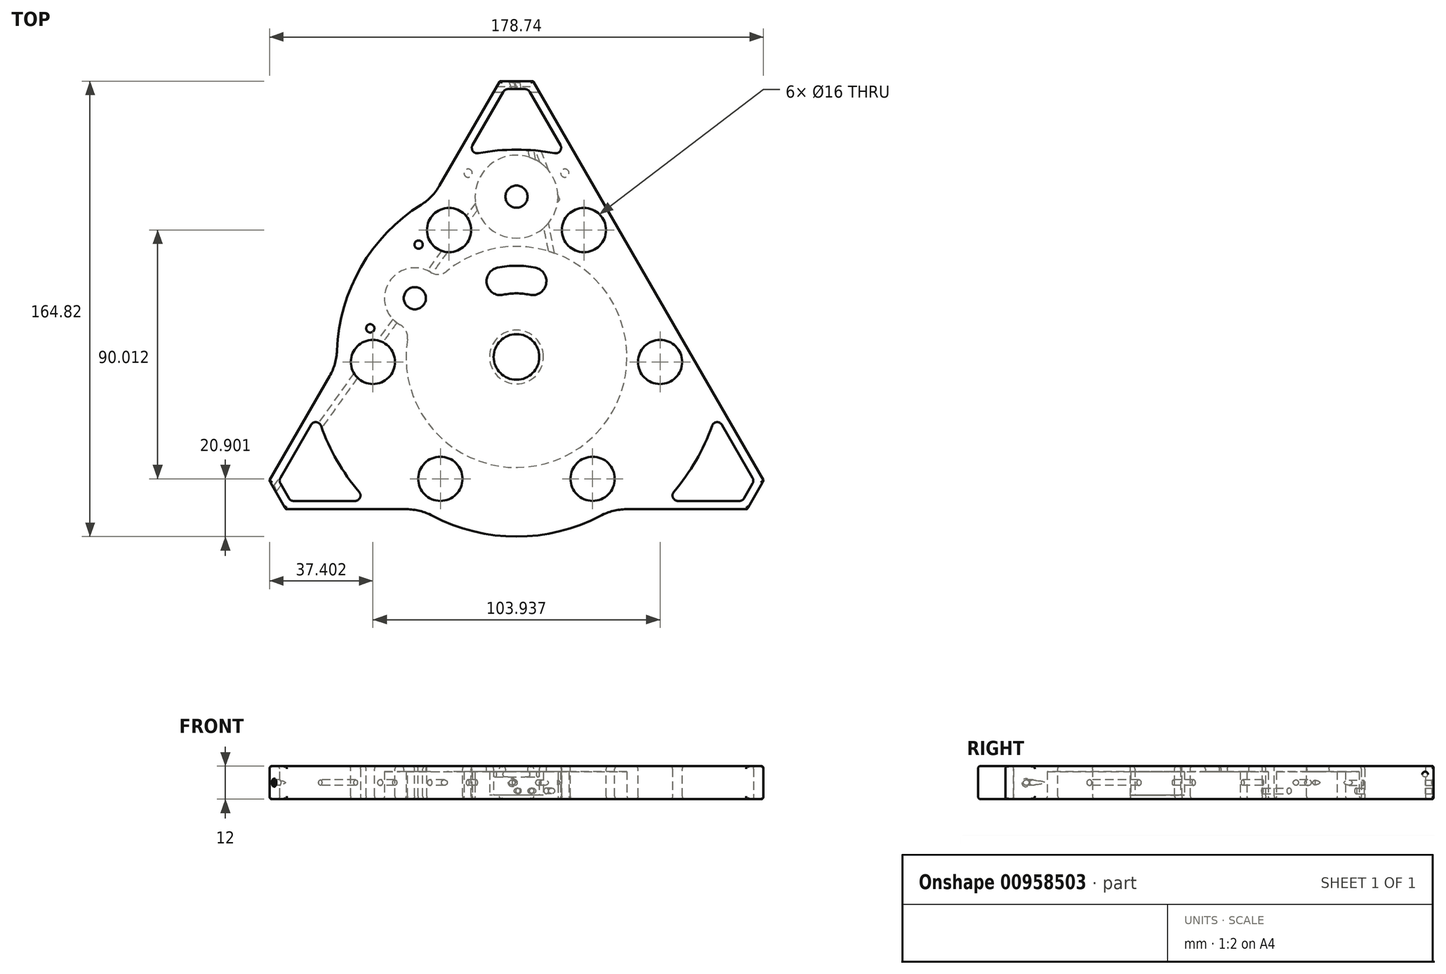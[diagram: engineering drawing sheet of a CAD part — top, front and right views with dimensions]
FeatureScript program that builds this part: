
annotation { "Feature Type Name" : "Feature", "Feature Type Description" : "" }
export const myFeature = defineFeature(function(context is Context, id is Id, definition is map)
    precondition{}
    {
        {
            var Q0;
            Q0=qCreatedBy(makeId("Top.planeOp"),FACE);
            var sketch = newSketch(context, id + "F0", { "sketchPlane" : qUnion([Q0])});
            skCircle(sketch, "E0", {"center": v(0, 0) * mm, "radius": 100 * mm, "construction": true});
            skCircle(sketch, "E1", {"center": v(0, 0) * mm, "radius": 65 * mm});
            skLineSegment(sketch, "E2", {"start": v(-6, 99.82) * mm, "end": v(-89.45, -44.71) * mm});
            skLineSegment(sketch, "E3", {"start": v(-89.45, -44.71) * mm, "end": v(-83.45, -55.1) * mm});
            skLineSegment(sketch, "E4", {"start": v(-83.45, -55.1) * mm, "end": v(83.45, -55.1) * mm});
            skLineSegment(sketch, "E5", {"start": v(83.45, -55.1) * mm, "end": v(89.45, -44.71) * mm});
            skLineSegment(sketch, "E6", {"start": v(89.45, -44.71) * mm, "end": v(6, 99.82) * mm});
            skLineSegment(sketch, "E7", {"start": v(6, 99.82) * mm, "end": v(-6, 99.82) * mm});
            skLineSegment(sketch, "E8", {"start": v(-86.6, -50) * mm, "end": v(0, 0) * mm, "construction": true});
            skLineSegment(sketch, "E9", {"start": v(0, 0) * mm, "end": v(86.45, -49.9) * mm, "construction": true});
            skCircle(sketch, "E10", {"center": v(0, 0) * mm, "radius": 75 * mm});
            skCircle(sketch, "E11", {"center": v(0, 0) * mm, "radius": 97 * mm, "construction": true});
            skLineSegment(sketch, "E12", {"start": v(-81.82, -52.1) * mm, "end": v(-53.94, -52.1) * mm});
            skLineSegment(sketch, "E13", {"start": v(-86.03, -44.8) * mm, "end": v(-72.1, -20.66) * mm});
            skLineSegment(sketch, "E14", {"start": v(-81.82, -52.1) * mm, "end": v(-86.03, -44.8) * mm});
            skLineSegment(sketch, "E15", {"start": v(81.82, -52.1) * mm, "end": v(53.94, -52.1) * mm});
            skLineSegment(sketch, "E16", {"start": v(86.03, -44.8) * mm, "end": v(72.1, -20.66) * mm});
            skLineSegment(sketch, "E17", {"start": v(86.03, -44.8) * mm, "end": v(81.82, -52.1) * mm});
            skLineSegment(sketch, "E18", {"start": v(-18.15, 72.77) * mm, "end": v(-4.22, 96.9) * mm});
            skLineSegment(sketch, "E19", {"start": v(18.15, 72.77) * mm, "end": v(4.22, 96.9) * mm});
            skLineSegment(sketch, "E20", {"start": v(4.22, 96.9) * mm, "end": v(-4.22, 96.9) * mm});
            skSolve(sketch);
        }
        {
            var Q0;
            {var subQ0=sQuery(id+"F0.wireOp",EDGE,"E2");var subQ1=sQuery(id+"F0.wireOp",EDGE,"E1");var subQ2=makeQuery(id+"F0.imprint","INTERSECT",VERTEX,{"disambiguationData":[OD(0.0)],"derivedFrom":[subQ1,subQ0]});Q0=makeQuery(id+"F0.imprint","IMPRINT",FACE,{"disambiguationData":[TD([[makeQuery(id+"F0.imprint","IMPRINT",EDGE,{"disambiguationData":[TD([[subQ2,1.0]])],"derivedFrom":subQ1}),1.0]])]});}
            var Q1;
            {var subQ2=sQuery(id+"F0.wireOp",EDGE,"E2");var subQ6=sQuery(id+"F0.wireOp",EDGE,"E1");var subQ8=makeQuery(id+"F0.imprint","INTERSECT",VERTEX,{"disambiguationData":[OD(1.0)],"derivedFrom":[subQ6,subQ2]});Q1=makeQuery(id+"F0.imprint","IMPRINT",FACE,{"disambiguationData":[TD([[makeQuery(id+"F0.imprint","IMPRINT",EDGE,{"disambiguationData":[TD([[subQ8,-1.0]])],"derivedFrom":subQ6}),-1.0]])]});}
            var Q2;
            {var subQ0=sQuery(id+"F0.wireOp",EDGE,"E4");var subQ1=sQuery(id+"F0.wireOp",EDGE,"E1");var subQ2=makeQuery(id+"F0.imprint","INTERSECT",VERTEX,{"disambiguationData":[OD(0.0)],"derivedFrom":[subQ1,subQ0]});Q2=makeQuery(id+"F0.imprint","IMPRINT",FACE,{"disambiguationData":[TD([[makeQuery(id+"F0.imprint","IMPRINT",EDGE,{"disambiguationData":[TD([[subQ2,-1.0]])],"derivedFrom":subQ1}),1.0]])]});}
            var Q3;
            {var subQ5=sQuery(id+"F0.wireOp",EDGE,"E3");Q3=makeQuery(id+"F0.imprint","IMPRINT",FACE,{"disambiguationData":[TD([[makeQuery(id+"F0.imprint","IMPRINT",EDGE,{"derivedFrom":subQ5}),1.0]])]});}
            var Q4;
            {var subQ0=sQuery(id+"F0.wireOp",EDGE,"E2");var subQ1=sQuery(id+"F0.wireOp",EDGE,"E1");var subQ2=makeQuery(id+"F0.imprint","INTERSECT",VERTEX,{"disambiguationData":[OD(0.0)],"derivedFrom":[subQ1,subQ0]});Q4=makeQuery(id+"F0.imprint","IMPRINT",FACE,{"disambiguationData":[TD([[makeQuery(id+"F0.imprint","IMPRINT",EDGE,{"disambiguationData":[TD([[subQ2,-1.0]])],"derivedFrom":subQ1}),1.0]])]});}
            var Q5;
            {var subQ4=sQuery(id+"F0.wireOp",EDGE,"E7");Q5=makeQuery(id+"F0.imprint","IMPRINT",FACE,{"disambiguationData":[TD([[makeQuery(id+"F0.imprint","IMPRINT",EDGE,{"derivedFrom":subQ4}),1.0]])]});}
            var Q6;
            {var subQ4=sQuery(id+"F0.wireOp",EDGE,"E1");var subQ6=sQuery(id+"F0.wireOp",EDGE,"E2");var subQ8=makeQuery(id+"F0.imprint","INTERSECT",VERTEX,{"disambiguationData":[OD(0.0)],"derivedFrom":[subQ4,subQ6]});Q6=makeQuery(id+"F0.imprint","IMPRINT",FACE,{"disambiguationData":[TD([[makeQuery(id+"F0.imprint","IMPRINT",EDGE,{"disambiguationData":[TD([[subQ8,1.0]])],"derivedFrom":subQ4}),-1.0]])]});}
            var Q7;
            {var subQ1=sQuery(id+"F0.wireOp",EDGE,"E5");Q7=makeQuery(id+"F0.imprint","IMPRINT",FACE,{"disambiguationData":[TD([[makeQuery(id+"F0.imprint","IMPRINT",EDGE,{"derivedFrom":subQ1}),1.0]])]});}
            var Q8;
            {var subQ2=sQuery(id+"F0.wireOp",EDGE,"E4");var subQ4=sQuery(id+"F0.wireOp",EDGE,"E1");var subQ5=makeQuery(id+"F0.imprint","INTERSECT",VERTEX,{"disambiguationData":[OD(1.0)],"derivedFrom":[subQ4,subQ2]});Q8=makeQuery(id+"F0.imprint","IMPRINT",FACE,{"disambiguationData":[TD([[makeQuery(id+"F0.imprint","IMPRINT",EDGE,{"disambiguationData":[TD([[subQ5,-1.0]])],"derivedFrom":subQ4}),-1.0]])]});}
            var Q9;
            {var subQ0=sQuery(id+"F0.wireOp",EDGE,"E6");var subQ1=sQuery(id+"F0.wireOp",EDGE,"E1");var subQ2=makeQuery(id+"F0.imprint","INTERSECT",VERTEX,{"disambiguationData":[OD(0.0)],"derivedFrom":[subQ1,subQ0]});Q9=makeQuery(id+"F0.imprint","IMPRINT",FACE,{"disambiguationData":[TD([[makeQuery(id+"F0.imprint","IMPRINT",EDGE,{"disambiguationData":[TD([[subQ2,1.0]])],"derivedFrom":subQ1}),1.0]])]});}
            extrude(context, id + "F1", {"entities" : qUnion([Q0, Q1, Q2, Q3, Q4, Q5, Q6, Q7, Q8, Q9]), "depth" : 12 * mm, "offsetDistance" : 25 * mm});
        }
        {
            var Q0;
            Q0=makeQuery(id+"F1.opExtrude","SWEPT_EDGE",EDGE,{"disambiguationData":[OSD([sQuery(id+"F0.wireOp",EDGE,"E10"),sQuery(id+"F0.wireOp",EDGE,"E13")])]});
            var Q1;
            Q1=makeQuery(id+"F1.opExtrude","SWEPT_EDGE",EDGE,{"disambiguationData":[OSD([sQuery(id+"F0.wireOp",EDGE,"E10"),sQuery(id+"F0.wireOp",EDGE,"E12")])]});
            var Q2;
            Q2=makeQuery(id+"F1.opExtrude","SWEPT_EDGE",EDGE,{"disambiguationData":[OSD([sQuery(id+"F0.wireOp",EDGE,"E13"),sQuery(id+"F0.wireOp",EDGE,"E14")])]});
            var Q3;
            Q3=makeQuery(id+"F1.opExtrude","SWEPT_EDGE",EDGE,{"disambiguationData":[OSD([sQuery(id+"F0.wireOp",EDGE,"E12"),sQuery(id+"F0.wireOp",EDGE,"E14")])]});
            var Q4;
            Q4=makeQuery(id+"F1.opExtrude","SWEPT_EDGE",EDGE,{"disambiguationData":[OSD([sQuery(id+"F0.wireOp",EDGE,"E10"),sQuery(id+"F0.wireOp",EDGE,"E18")])]});
            var Q5;
            Q5=makeQuery(id+"F1.opExtrude","SWEPT_EDGE",EDGE,{"disambiguationData":[OSD([sQuery(id+"F0.wireOp",EDGE,"E10"),sQuery(id+"F0.wireOp",EDGE,"E19")])]});
            var Q6;
            Q6=makeQuery(id+"F1.opExtrude","SWEPT_EDGE",EDGE,{"disambiguationData":[OSD([sQuery(id+"F0.wireOp",EDGE,"E19"),sQuery(id+"F0.wireOp",EDGE,"E20")])]});
            var Q7;
            Q7=makeQuery(id+"F1.opExtrude","SWEPT_EDGE",EDGE,{"disambiguationData":[OSD([sQuery(id+"F0.wireOp",EDGE,"E18"),sQuery(id+"F0.wireOp",EDGE,"E20")])]});
            var Q8;
            Q8=makeQuery(id+"F1.opExtrude","SWEPT_EDGE",EDGE,{"disambiguationData":[OSD([sQuery(id+"F0.wireOp",EDGE,"E10"),sQuery(id+"F0.wireOp",EDGE,"E16")])]});
            var Q9;
            Q9=makeQuery(id+"F1.opExtrude","SWEPT_EDGE",EDGE,{"disambiguationData":[OSD([sQuery(id+"F0.wireOp",EDGE,"E10"),sQuery(id+"F0.wireOp",EDGE,"E15")])]});
            var Q10;
            Q10=makeQuery(id+"F1.opExtrude","SWEPT_EDGE",EDGE,{"disambiguationData":[OSD([sQuery(id+"F0.wireOp",EDGE,"E15"),sQuery(id+"F0.wireOp",EDGE,"E17")])]});
            var Q11;
            Q11=makeQuery(id+"F1.opExtrude","SWEPT_EDGE",EDGE,{"disambiguationData":[OSD([sQuery(id+"F0.wireOp",EDGE,"E16"),sQuery(id+"F0.wireOp",EDGE,"E17")])]});
            fillet(context, id + "F2", {"entities" : qUnion([Q0, Q1, Q2, Q3, Q4, Q5, Q6, Q7, Q8, Q9, Q10, Q11]), "radius" : 2 * mm, "tangentPropagation" : true, "allowEdgeOverflow" : false});
        }
        {
            var Q0;
            Q0=qCreatedBy(makeId("Top.planeOp"),FACE);
            var sketch = newSketch(context, id + "F3", { "sketchPlane" : qUnion([Q0])});
            skCircle(sketch, "E21", {"center": v(0, 0) * mm, "radius": 8.25 * mm});
            skSolve(sketch);
        }
        {
            var Q0;
            Q0=qSketchRegion(id+"F3",true);
            extrude(context, id + "F4", {"entities" : qUnion([Q0]), "operationType" : NewBodyOperationType.REMOVE, "depth" : 100 * mm, "offsetDistance" : 25 * mm});
        }
        {
            var Q0;
            Q0=qCreatedBy(makeId("Top.planeOp"),FACE);
            var sketch = newSketch(context, id + "F5", { "sketchPlane" : qUnion([Q0])});
            skCircle(sketch, "E22", {"center": v(0, 58) * mm, "radius": 15 * mm});
            skCircle(sketch, "E23", {"center": v(-17.5, 66.5) * mm, "radius": 1.5 * mm});
            skCircle(sketch, "E24", {"center": v(17.5, 66.5) * mm, "radius": 1.5 * mm});
            skCircle(sketch, "E25", {"center": v(0, 58) * mm, "radius": 4 * mm});
            skSolve(sketch);
        }
        {
            var Q0;
            Q0=makeQuery(id+"F5.imprint","IMPRINT",FACE,{"disambiguationData":[TD([[makeQuery(id+"F5.imprint","IMPRINT",EDGE,{"derivedFrom":sQuery(id+"F5.wireOp",EDGE,"E25")}),1.0]])]});
            var Q1;
            Q1=makeQuery(id+"F5.imprint","IMPRINT",FACE,{"disambiguationData":[TD([[makeQuery(id+"F5.imprint","IMPRINT",EDGE,{"derivedFrom":sQuery(id+"F5.wireOp",EDGE,"E22")}),1.0]])]});
            var Q2;
            Q2=makeQuery(id+"F5.imprint","IMPRINT",FACE,{"disambiguationData":[TD([[makeQuery(id+"F5.imprint","IMPRINT",EDGE,{"derivedFrom":sQuery(id+"F5.wireOp",EDGE,"E24")}),1.0]])]});
            var Q3;
            Q3=makeQuery(id+"F5.imprint","IMPRINT",FACE,{"disambiguationData":[TD([[makeQuery(id+"F5.imprint","IMPRINT",EDGE,{"derivedFrom":sQuery(id+"F5.wireOp",EDGE,"E23")}),1.0]])]});
            extrude(context, id + "F6", {"entities" : qUnion([Q0, Q1, Q2, Q3]), "operationType" : NewBodyOperationType.REMOVE, "depth" : 10 * mm, "offsetDistance" : 25 * mm});
        }
        {
            var Q0;
            Q0=makeQuery(id+"F5.imprint","IMPRINT",FACE,{"disambiguationData":[TD([[makeQuery(id+"F5.imprint","IMPRINT",EDGE,{"derivedFrom":sQuery(id+"F5.wireOp",EDGE,"E25")}),1.0]])]});
            extrude(context, id + "F7", {"entities" : qUnion([Q0]), "operationType" : NewBodyOperationType.REMOVE, "depth" : 25 * mm, "offsetDistance" : 25 * mm});
        }
        {
            var Q0;
            Q0=qCreatedBy(makeId("Top.planeOp"),FACE);
            var sketch = newSketch(context, id + "F8", { "sketchPlane" : qUnion([Q0])});
            skCircle(sketch, "E26", {"center": v(0, 0) * mm, "radius": 40 * mm});
            skCircle(sketch, "E27", {"center": v(0, 0) * mm, "radius": 9.75 * mm});
            skSolve(sketch);
        }
        {
            var Q0;
            Q0=qSketchRegion(id+"F8",true);
            extrude(context, id + "F9", {"entities" : qUnion([Q0]), "operationType" : NewBodyOperationType.REMOVE, "depth" : 10 * mm, "offsetDistance" : 25 * mm});
        }
        {
            var Q0;
            Q0=qCreatedBy(makeId("Top.planeOp"),FACE);
            var sketch = newSketch(context, id + "F10", { "sketchPlane" : qUnion([Q0])});
            skCircle(sketch, "E28", {"center": v(-36.8, 21.25) * mm, "radius": 11 * mm});
            skLineSegment(sketch, "E29", {"start": v(-36.8, 21.25) * mm, "end": v(0, 0) * mm, "construction": true});
            skCircle(sketch, "E30", {"center": v(-36.8, 21.25) * mm, "radius": 4 * mm});
            skSolve(sketch);
        }
        {
            var Q0;
            Q0=makeQuery(id+"F10.imprint","IMPRINT",FACE,{"disambiguationData":[TD([[makeQuery(id+"F10.imprint","IMPRINT",EDGE,{"derivedFrom":sQuery(id+"F10.wireOp",EDGE,"E28")}),1.0]])]});
            var Q1;
            Q1=makeQuery(id+"F10.imprint","IMPRINT",FACE,{"disambiguationData":[TD([[makeQuery(id+"F10.imprint","IMPRINT",EDGE,{"derivedFrom":sQuery(id+"F10.wireOp",EDGE,"E30")}),1.0]])]});
            extrude(context, id + "F11", {"entities" : qUnion([Q0, Q1]), "operationType" : NewBodyOperationType.REMOVE, "depth" : 10 * mm, "offsetDistance" : 25 * mm});
        }
        {
            var Q0;
            Q0=makeQuery(id+"F10.imprint","IMPRINT",FACE,{"disambiguationData":[TD([[makeQuery(id+"F10.imprint","IMPRINT",EDGE,{"derivedFrom":sQuery(id+"F10.wireOp",EDGE,"E30")}),1.0]])]});
            extrude(context, id + "F12", {"entities" : qUnion([Q0]), "operationType" : NewBodyOperationType.REMOVE, "depth" : 25 * mm, "offsetDistance" : 25 * mm});
        }
        {
            var Q0;
            Q0=qCreatedBy(makeId("Top.planeOp"),FACE);
            var sketch = newSketch(context, id + "F13", { "sketchPlane" : qUnion([Q0])});
            skLineSegment(sketch, "E31", {"start": v(0, 0) * mm, "end": v(-36.8, 21.25) * mm, "construction": true});
            skLineSegment(sketch, "E32", {"start": v(-35.42, 40.66) * mm, "end": v(-52.92, 10.34) * mm, "construction": true});
            skCircle(sketch, "E33", {"center": v(-35.42, 40.66) * mm, "radius": 1.5 * mm});
            skCircle(sketch, "E34", {"center": v(-52.92, 10.34) * mm, "radius": 1.5 * mm});
            skCircle(sketch, "E35", {"center": v(-35.42, 40.66) * mm, "radius": 4 * mm});
            skCircle(sketch, "E36", {"center": v(-52.92, 10.34) * mm, "radius": 4 * mm});
            skSolve(sketch);
        }
        {
            var Q0;
            Q0=makeQuery(id+"F13.imprint","IMPRINT",FACE,{"disambiguationData":[TD([[makeQuery(id+"F13.imprint","IMPRINT",EDGE,{"derivedFrom":sQuery(id+"F13.wireOp",EDGE,"E33")}),1.0]])]});
            var Q1;
            Q1=makeQuery(id+"F13.imprint","IMPRINT",FACE,{"disambiguationData":[TD([[makeQuery(id+"F13.imprint","IMPRINT",EDGE,{"derivedFrom":sQuery(id+"F13.wireOp",EDGE,"E34")}),1.0]])]});
            extrude(context, id + "F14", {"entities" : qUnion([Q0, Q1]), "operationType" : NewBodyOperationType.REMOVE, "endBound" : BoundingType.SYMMETRIC, "oppositeDirection" : true, "depth" : 100 * mm, "offsetDistance" : 25 * mm});
        }
        {
            var Q0;
            Q0=qCreatedBy(makeId("Top.planeOp"),FACE);
            cPlane(context, id + "F15", {"entities" : qUnion([Q0]), "cplaneType" : CPlaneType.OFFSET, "offset" : 3 * mm, "width" : 150 * mm, "height" : 150 * mm});
        }
        {
            var Q0;
            Q0=makeQuery(id+"F11.boolean.opBoolean","INTERSECT",EDGE,{"disambiguationData":[OD(1.0)],"derivedFrom":[makeQuery(id+"F9.boolean.opBoolean","COPY",FACE,{"derivedFrom":makeQuery(id+"F9.opExtrude","SWEPT_FACE",FACE,{"disambiguationData":[OSD([sQuery(id+"F8.wireOp",EDGE,"E26")])]})}),makeQuery(id+"F11.opExtrude","SWEPT_FACE",FACE,{"disambiguationData":[OSD([sQuery(id+"F10.wireOp",EDGE,"E28")])]})]});
            var Q1;
            Q1=makeQuery(id+"F11.boolean.opBoolean","INTERSECT",EDGE,{"disambiguationData":[OD(0.0)],"derivedFrom":[makeQuery(id+"F9.boolean.opBoolean","COPY",FACE,{"derivedFrom":makeQuery(id+"F9.opExtrude","SWEPT_FACE",FACE,{"disambiguationData":[OSD([sQuery(id+"F8.wireOp",EDGE,"E26")])]})}),makeQuery(id+"F11.opExtrude","SWEPT_FACE",FACE,{"disambiguationData":[OSD([sQuery(id+"F10.wireOp",EDGE,"E28")])]})]});
            var Q2;
            Q2=makeQuery(id+"FJ90VYnbGjNsUTn_1.2.F11.boolean.opBoolean","INTERSECT",EDGE,{"disambiguationData":[OD(0.0)],"derivedFrom":[makeQuery(id+"FJ90VYnbGjNsUTn_1.1.F11.boolean.opBoolean","SPLIT",FACE,{"disambiguationData":[OD(1.0)],"derivedFrom":makeQuery(id+"F9.boolean.opBoolean","COPY",FACE,{"derivedFrom":makeQuery(id+"F9.opExtrude","SWEPT_FACE",FACE,{"disambiguationData":[OSD([sQuery(id+"F8.wireOp",EDGE,"E26")])]})})}),makeQuery(id+"FJ90VYnbGjNsUTn_1.2.F11.opExtrude","SWEPT_FACE",FACE,{"disambiguationData":[OSD([sQuery(id+"F10.wireOp",EDGE,"E28")])]})]});
            var Q3;
            Q3=makeQuery(id+"FJ90VYnbGjNsUTn_1.2.F11.boolean.opBoolean","INTERSECT",EDGE,{"disambiguationData":[OD(1.0)],"derivedFrom":[makeQuery(id+"FJ90VYnbGjNsUTn_1.1.F11.boolean.opBoolean","SPLIT",FACE,{"disambiguationData":[OD(1.0)],"derivedFrom":makeQuery(id+"F9.boolean.opBoolean","COPY",FACE,{"derivedFrom":makeQuery(id+"F9.opExtrude","SWEPT_FACE",FACE,{"disambiguationData":[OSD([sQuery(id+"F8.wireOp",EDGE,"E26")])]})})}),makeQuery(id+"FJ90VYnbGjNsUTn_1.2.F11.opExtrude","SWEPT_FACE",FACE,{"disambiguationData":[OSD([sQuery(id+"F10.wireOp",EDGE,"E28")])]})]});
            var Q4;
            Q4=makeQuery(id+"FJ90VYnbGjNsUTn_1.1.F11.boolean.opBoolean","INTERSECT",EDGE,{"disambiguationData":[OD(1.0)],"derivedFrom":[makeQuery(id+"F9.boolean.opBoolean","COPY",FACE,{"derivedFrom":makeQuery(id+"F9.opExtrude","SWEPT_FACE",FACE,{"disambiguationData":[OSD([sQuery(id+"F8.wireOp",EDGE,"E26")])]})}),makeQuery(id+"FJ90VYnbGjNsUTn_1.1.F11.opExtrude","SWEPT_FACE",FACE,{"disambiguationData":[OSD([sQuery(id+"F10.wireOp",EDGE,"E28")])]})]});
            var Q5;
            Q5=makeQuery(id+"FJ90VYnbGjNsUTn_1.1.F11.boolean.opBoolean","INTERSECT",EDGE,{"disambiguationData":[OD(0.0)],"derivedFrom":[makeQuery(id+"F9.boolean.opBoolean","COPY",FACE,{"derivedFrom":makeQuery(id+"F9.opExtrude","SWEPT_FACE",FACE,{"disambiguationData":[OSD([sQuery(id+"F8.wireOp",EDGE,"E26")])]})}),makeQuery(id+"FJ90VYnbGjNsUTn_1.1.F11.opExtrude","SWEPT_FACE",FACE,{"disambiguationData":[OSD([sQuery(id+"F10.wireOp",EDGE,"E28")])]})]});
            fillet(context, id + "F16", {"entities" : qUnion([Q0, Q1, Q2, Q3, Q4, Q5]), "radius" : 5 * mm, "tangentPropagation" : true, "allowEdgeOverflow" : false});
        }
        {
            var Q0;
            Q0=qCreatedBy(id+"F15.planeOp",FACE);
            var sketch = newSketch(context, id + "F17", { "sketchPlane" : qUnion([Q0])});
            skCircle(sketch, "E37", {"center": v(0, 0) * mm, "radius": 20 * mm, "construction": true});
            skLineSegment(sketch, "E38", {"start": v(19.6, 3.98) * mm, "end": v(0, 100.5) * mm});
            skCircle(sketch, "E39", {"center": v(0, 0) * mm, "radius": 100.5 * mm, "construction": true});
            skLineSegment(sketch, "E40", {"start": v(19.6, 3.98) * mm, "end": v(20.58, 4.18) * mm});
            skLineSegment(sketch, "E41", {"start": v(20.58, 4.18) * mm, "end": v(0.98, 100.7) * mm});
            skLineSegment(sketch, "E42", {"start": v(0.98, 100.7) * mm, "end": v(0, 100.5) * mm});
            skSolve(sketch);
        }
        {
            var Q0;
            Q0=makeQuery(id+"F17.imprint","IMPRINT",FACE,{"disambiguationData":[TD([[makeQuery(id+"F17.imprint","IMPRINT",EDGE,{"derivedFrom":sQuery(id+"F17.wireOp",EDGE,"E38")}),-1.0]])]});
            var Q1;
            Q1=sQuery(id+"F17.wireOp",EDGE,"E38");
            revolve(context, id + "F18", {"operationType" : NewBodyOperationType.REMOVE, "surfaceOperationType" : NewSurfaceOperationType.NEW, "entities" : qUnion([Q0]), "axis" : qUnion([Q1]), "revolveType" : RevolveType.FULL, "oppositeDirection" : true});
        }
        {
            var Q0;
            Q0=qCreatedBy(makeId("Top.planeOp"),FACE);
            cPlane(context, id + "F19", {"entities" : qUnion([Q0]), "cplaneType" : CPlaneType.OFFSET, "offset" : 6 * mm, "width" : 150 * mm, "height" : 150 * mm});
        }
        {
            var Q0;
            Q0=qCreatedBy(id+"F19.planeOp",FACE);
            var sketch = newSketch(context, id + "F20", { "sketchPlane" : qUnion([Q0])});
            skCircle(sketch, "E43", {"center": v(0, 0) * mm, "radius": 58 * mm, "construction": true});
            skCircle(sketch, "E44", {"center": v(0, 0) * mm, "radius": 100.5 * mm, "construction": true});
            skLineSegment(sketch, "E45", {"start": v(15, 56.03) * mm, "end": v(-2, 100.48) * mm});
            skLineSegment(sketch, "E46", {"start": v(-2, 100.48) * mm, "end": v(-3, 100.46) * mm});
            skLineSegment(sketch, "E47", {"start": v(-3, 100.46) * mm, "end": v(13.88, 56.31) * mm});
            skLineSegment(sketch, "E48", {"start": v(13.88, 56.31) * mm, "end": v(15, 56.03) * mm});
            skLineSegment(sketch, "E49", {"start": v(-13, 56.52) * mm, "end": v(-88.02, -48.5) * mm});
            skLineSegment(sketch, "E50", {"start": v(-88.02, -48.5) * mm, "end": v(-88.55, -47.53) * mm});
            skLineSegment(sketch, "E51", {"start": v(-88.55, -47.53) * mm, "end": v(-14.49, 56.16) * mm});
            skLineSegment(sketch, "E52", {"start": v(-13, 56.52) * mm, "end": v(-14.49, 56.16) * mm});
            skLineSegment(sketch, "E53", {"start": v(0, 0) * mm, "end": v(-87.04, -50.25) * mm, "construction": true});
            skSolve(sketch);
        }
        {
            var Q0;
            Q0=makeQuery(id+"F20.imprint","IMPRINT",FACE,{"disambiguationData":[TD([[makeQuery(id+"F20.imprint","IMPRINT",EDGE,{"derivedFrom":sQuery(id+"F20.wireOp",EDGE,"E45")}),1.0]])]});
            var Q1;
            Q1=sQuery(id+"F20.wireOp",EDGE,"E45");
            revolve(context, id + "F21", {"operationType" : NewBodyOperationType.REMOVE, "surfaceOperationType" : NewSurfaceOperationType.NEW, "entities" : qUnion([Q0]), "axis" : qUnion([Q1]), "revolveType" : RevolveType.FULL, "oppositeDirection" : true});
        }
        {
            var Q0;
            Q0=makeQuery(id+"F20.imprint","IMPRINT",FACE,{"disambiguationData":[TD([[makeQuery(id+"F20.imprint","IMPRINT",EDGE,{"derivedFrom":sQuery(id+"F20.wireOp",EDGE,"E49")}),-1.0]])]});
            var Q1;
            Q1=sQuery(id+"F20.wireOp",EDGE,"E49");
            revolve(context, id + "F22", {"operationType" : NewBodyOperationType.REMOVE, "surfaceOperationType" : NewSurfaceOperationType.NEW, "entities" : qUnion([Q0]), "axis" : qUnion([Q1]), "revolveType" : RevolveType.FULL, "oppositeDirection" : true});
        }
        {
            var Q0;
            Q0=qCreatedBy(makeId("Top.planeOp"),FACE);
            var sketch = newSketch(context, id + "F23", { "sketchPlane" : qUnion([Q0])});
            skCircle(sketch, "E54", {"center": v(0, 0) * mm, "radius": 10 * mm});
            skSolve(sketch);
        }
        {
            var Q0;
            Q0=makeQuery(id+"F23.imprint","IMPRINT",FACE,{"disambiguationData":[TD([[makeQuery(id+"F23.imprint","IMPRINT",EDGE,{"derivedFrom":sQuery(id+"F23.wireOp",EDGE,"E54")}),1.0]])]});
            extrude(context, id + "F24", {"entities" : qUnion([Q0]), "operationType" : NewBodyOperationType.REMOVE, "depth" : 1.5 * mm, "offsetDistance" : 25 * mm});
        }
        {
            var Q0;
            Q0=qCreatedBy(makeId("Right.planeOp"),FACE);
            var sketch = newSketch(context, id + "F25", { "sketchPlane" : qUnion([Q0])});
            skCircle(sketch, "E55", {"center": v(96.82, 9) * mm, "radius": 1 * mm});
            skSolve(sketch);
        }
        {
            var Q0;
            Q0=qSketchRegion(id+"F25",true);
            extrude(context, id + "F26", {"entities" : qUnion([Q0]), "operationType" : NewBodyOperationType.REMOVE, "endBound" : BoundingType.SYMMETRIC, "oppositeDirection" : true, "depth" : 25 * mm, "offsetDistance" : 25 * mm});
        }
        {
            var Q0;
            {var subQ0=sQuery(id+"F0.wireOp",EDGE,"E2");var subQ1=sQuery(id+"F0.wireOp",EDGE,"E1");Q0=makeQuery(id+"F1.opExtrude","SWEPT_EDGE",EDGE,{"disambiguationData":[OSD([subQ1,subQ0]),TDD([makeQuery(id+"F0.imprint","INTERSECT",VERTEX,{"disambiguationData":[OD(0.0)],"derivedFrom":[subQ1,subQ0]})])]});}
            var Q1;
            {var subQ0=sQuery(id+"F0.wireOp",EDGE,"E2");var subQ1=sQuery(id+"F0.wireOp",EDGE,"E1");Q1=makeQuery(id+"F1.opExtrude","SWEPT_EDGE",EDGE,{"disambiguationData":[OSD([subQ1,subQ0]),TDD([makeQuery(id+"F0.imprint","INTERSECT",VERTEX,{"disambiguationData":[OD(1.0)],"derivedFrom":[subQ1,subQ0]})])]});}
            var Q2;
            {var subQ0=sQuery(id+"F0.wireOp",EDGE,"E4");var subQ1=sQuery(id+"F0.wireOp",EDGE,"E1");Q2=makeQuery(id+"F1.opExtrude","SWEPT_EDGE",EDGE,{"disambiguationData":[OSD([subQ1,subQ0]),TDD([makeQuery(id+"F0.imprint","INTERSECT",VERTEX,{"disambiguationData":[OD(0.0)],"derivedFrom":[subQ1,subQ0]})])]});}
            var Q3;
            {var subQ0=sQuery(id+"F0.wireOp",EDGE,"E4");var subQ1=sQuery(id+"F0.wireOp",EDGE,"E1");Q3=makeQuery(id+"F1.opExtrude","SWEPT_EDGE",EDGE,{"disambiguationData":[OSD([subQ1,subQ0]),TDD([makeQuery(id+"F0.imprint","INTERSECT",VERTEX,{"disambiguationData":[OD(1.0)],"derivedFrom":[subQ1,subQ0]})])]});}
            var Q4;
            {var subQ0=sQuery(id+"F0.wireOp",EDGE,"E6");var subQ1=sQuery(id+"F0.wireOp",EDGE,"E1");Q4=makeQuery(id+"F1.opExtrude","SWEPT_EDGE",EDGE,{"disambiguationData":[OSD([subQ1,subQ0]),TDD([makeQuery(id+"F0.imprint","INTERSECT",VERTEX,{"disambiguationData":[OD(1.0)],"derivedFrom":[subQ1,subQ0]})])]});}
            var Q5;
            {var subQ0=sQuery(id+"F0.wireOp",EDGE,"E6");var subQ1=sQuery(id+"F0.wireOp",EDGE,"E1");Q5=makeQuery(id+"F1.opExtrude","SWEPT_EDGE",EDGE,{"disambiguationData":[OSD([subQ1,subQ0]),TDD([makeQuery(id+"F0.imprint","INTERSECT",VERTEX,{"disambiguationData":[OD(0.0)],"derivedFrom":[subQ1,subQ0]})])]});}
            fillet(context, id + "F27", {"entities" : qUnion([Q0, Q1, Q2, Q3, Q4, Q5]), "radius" : 20 * mm, "tangentPropagation" : true, "allowEdgeOverflow" : false});
        }
        {
            var Q0;
            Q0=makeQuery(id+"F1.opExtrude","SWEPT_FACE",FACE,{"disambiguationData":[OSD([sQuery(id+"F0.wireOp",EDGE,"E7")])]});
            var Q1;
            Q1=makeQuery(id+"F1.opExtrude","SWEPT_FACE",FACE,{"disambiguationData":[OSD([sQuery(id+"F0.wireOp",EDGE,"E3")])]});
            var Q2;
            Q2=makeQuery(id+"F1.opExtrude","SWEPT_FACE",FACE,{"disambiguationData":[OSD([sQuery(id+"F0.wireOp",EDGE,"E5")])]});
            fillet(context, id + "F28", {"entities" : qUnion([Q0, Q1, Q2]), "radius" : 0.5 * mm, "tangentPropagation" : true, "allowEdgeOverflow" : false});
        }
        {
            var Q0;
            Q0=qCreatedBy(makeId("Top.planeOp"),FACE);
            var sketch = newSketch(context, id + "F29", { "sketchPlane" : qUnion([Q0])});
            skCircle(sketch, "E56", {"center": v(0, 0) * mm, "radius": 52 * mm, "construction": true});
            skCircle(sketch, "E57", {"center": v(24.41, 45.91) * mm, "radius": 8 * mm});
            skCircle(sketch, "E58", {"center": v(51.97, -1.81) * mm, "radius": 8 * mm});
            skCircle(sketch, "E59", {"center": v(27.56, -44.1) * mm, "radius": 8 * mm});
            skCircle(sketch, "E60", {"center": v(-27.56, -44.1) * mm, "radius": 8 * mm});
            skLineSegment(sketch, "E61", {"start": v(-27.56, -44.1) * mm, "end": v(0, 0) * mm, "construction": true});
            skLineSegment(sketch, "E62", {"start": v(27.56, -44.1) * mm, "end": v(0, 0) * mm, "construction": true});
            skLineSegment(sketch, "E63", {"start": v(51.97, -1.81) * mm, "end": v(0, 0) * mm, "construction": true});
            skLineSegment(sketch, "E64", {"start": v(24.41, 45.91) * mm, "end": v(0, 0) * mm, "construction": true});
            skCircle(sketch, "E65", {"center": v(47.87, 20.32) * mm, "radius": 8 * mm, "construction": true});
            skLineSegment(sketch, "E66", {"start": v(47.87, 20.32) * mm, "end": v(0, 0) * mm, "construction": true});
            skCircle(sketch, "E67", {"center": v(-24.41, 45.91) * mm, "radius": 8 * mm});
            skCircle(sketch, "E68", {"center": v(-51.97, -1.81) * mm, "radius": 8 * mm});
            skLineSegment(sketch, "E69", {"start": v(0, 0) * mm, "end": v(-51.97, -1.81) * mm, "construction": true});
            skLineSegment(sketch, "E70", {"start": v(-24.41, 45.91) * mm, "end": v(0, 0) * mm, "construction": true});
            skSolve(sketch);
        }
        {
            var Q0;
            Q0=qSketchRegion(id+"F29",true);
            extrude(context, id + "F30", {"entities" : qUnion([Q0]), "operationType" : NewBodyOperationType.REMOVE, "endBound" : BoundingType.SYMMETRIC, "oppositeDirection" : true, "depth" : 100 * mm, "offsetDistance" : 25 * mm});
        }
        {
            var Q0;
            Q0=qCreatedBy(makeId("Top.planeOp"),FACE);
            var sketch = newSketch(context, id + "F31", { "sketchPlane" : qUnion([Q0])});
            skCircle(sketch, "E71", {"center": v(0, 0) * mm, "radius": 28 * mm, "construction": true});
            skCircle(sketch, "E72", {"center": v(5.82, 27.39) * mm, "radius": 5 * mm});
            skCircle(sketch, "E73", {"center": v(-5.82, 27.39) * mm, "radius": 5 * mm});
            skCircle(sketch, "E74", {"center": v(0, 0) * mm, "radius": 23 * mm});
            skCircle(sketch, "E75", {"center": v(0, 0) * mm, "radius": 33 * mm});
            skLineSegment(sketch, "E76", {"start": v(5.82, 27.39) * mm, "end": v(0, 0) * mm, "construction": true});
            skLineSegment(sketch, "E77", {"start": v(-5.82, 27.39) * mm, "end": v(0, 0) * mm, "construction": true});
            skSolve(sketch);
        }
        {
            var Q0;
            {var subQ0=sQuery(id+"F31.wireOp",EDGE,"E75");var subQ1=sQuery(id+"F31.wireOp",EDGE,"E72");var subQ2=makeQuery(id+"F31.imprint","INTERSECT",VERTEX,{"derivedFrom":[subQ1,subQ0]});Q0=makeQuery(id+"F31.imprint","IMPRINT",FACE,{"disambiguationData":[TD([[makeQuery(id+"F31.imprint","IMPRINT",EDGE,{"disambiguationData":[TD([[subQ2,-1.0]])],"derivedFrom":subQ1}),-1.0]])]});}
            var Q1;
            {var subQ0=sQuery(id+"F31.wireOp",EDGE,"E72");var subQ1=makeQuery(id+"F31.imprint","INTERSECT",VERTEX,{"derivedFrom":[subQ0,sQuery(id+"F31.wireOp",EDGE,"E75")]});Q1=makeQuery(id+"F31.imprint","IMPRINT",FACE,{"disambiguationData":[TD([[makeQuery(id+"F31.imprint","IMPRINT",EDGE,{"disambiguationData":[TD([[subQ1,-1.0]])],"derivedFrom":subQ0}),1.0]])]});}
            var Q2;
            {var subQ0=sQuery(id+"F31.wireOp",EDGE,"E73");var subQ1=makeQuery(id+"F31.imprint","INTERSECT",VERTEX,{"derivedFrom":[subQ0,sQuery(id+"F31.wireOp",EDGE,"E75")]});Q2=makeQuery(id+"F31.imprint","IMPRINT",FACE,{"disambiguationData":[TD([[makeQuery(id+"F31.imprint","IMPRINT",EDGE,{"disambiguationData":[TD([[subQ1,-1.0]])],"derivedFrom":subQ0}),1.0]])]});}
            extrude(context, id + "F32", {"entities" : qUnion([Q0, Q1, Q2]), "operationType" : NewBodyOperationType.REMOVE, "endBound" : BoundingType.SYMMETRIC, "oppositeDirection" : true, "depth" : 100 * mm, "offsetDistance" : 25 * mm});
        }
        {
            var Q0;
            Q0=makeQuery(id+"F1.opExtrude","CAP_FACE",FACE,{"disambiguationData":[OSD([sQuery(id+"F0.wireOp",EDGE,"E1"),sQuery(id+"F0.wireOp",EDGE,"E2"),sQuery(id+"F0.wireOp",EDGE,"E3"),sQuery(id+"F0.wireOp",EDGE,"E4"),sQuery(id+"F0.wireOp",EDGE,"E5"),sQuery(id+"F0.wireOp",EDGE,"E6"),sQuery(id+"F0.wireOp",EDGE,"E7")])],"isStart":false});
            var Q1;
            {var subQ0=sQuery(id+"F0.wireOp",EDGE,"E5");var subQ1=sQuery(id+"F0.wireOp",EDGE,"E4");var subQ2=sQuery(id+"F0.wireOp",EDGE,"E1");var subQ4=sQuery(id+"F0.wireOp",EDGE,"E3");var subQ7=sQuery(id+"F0.wireOp",EDGE,"E2");var subQ9=sQuery(id+"F0.wireOp",EDGE,"E6");var subQ13=sQuery(id+"F0.wireOp",EDGE,"E7");Q1=makeQuery(id+"F9.boolean.opBoolean","SPLIT",FACE,{"disambiguationData":[TD([makeQuery(id+"F1.opExtrude","SWEPT_FACE",FACE,{"disambiguationData":[OSD([subQ4])]})])],"derivedFrom":makeQuery(id+"F1.opExtrude","CAP_FACE",FACE,{"disambiguationData":[OSD([subQ2,subQ7,subQ4,subQ1,subQ0,subQ9,subQ13])],"isStart":true})});}
            fillet(context, id + "F33", {"entities" : qUnion([Q0, Q1]), "radius" : 1 * mm, "tangentPropagation" : true, "allowEdgeOverflow" : false});
        }
    });
